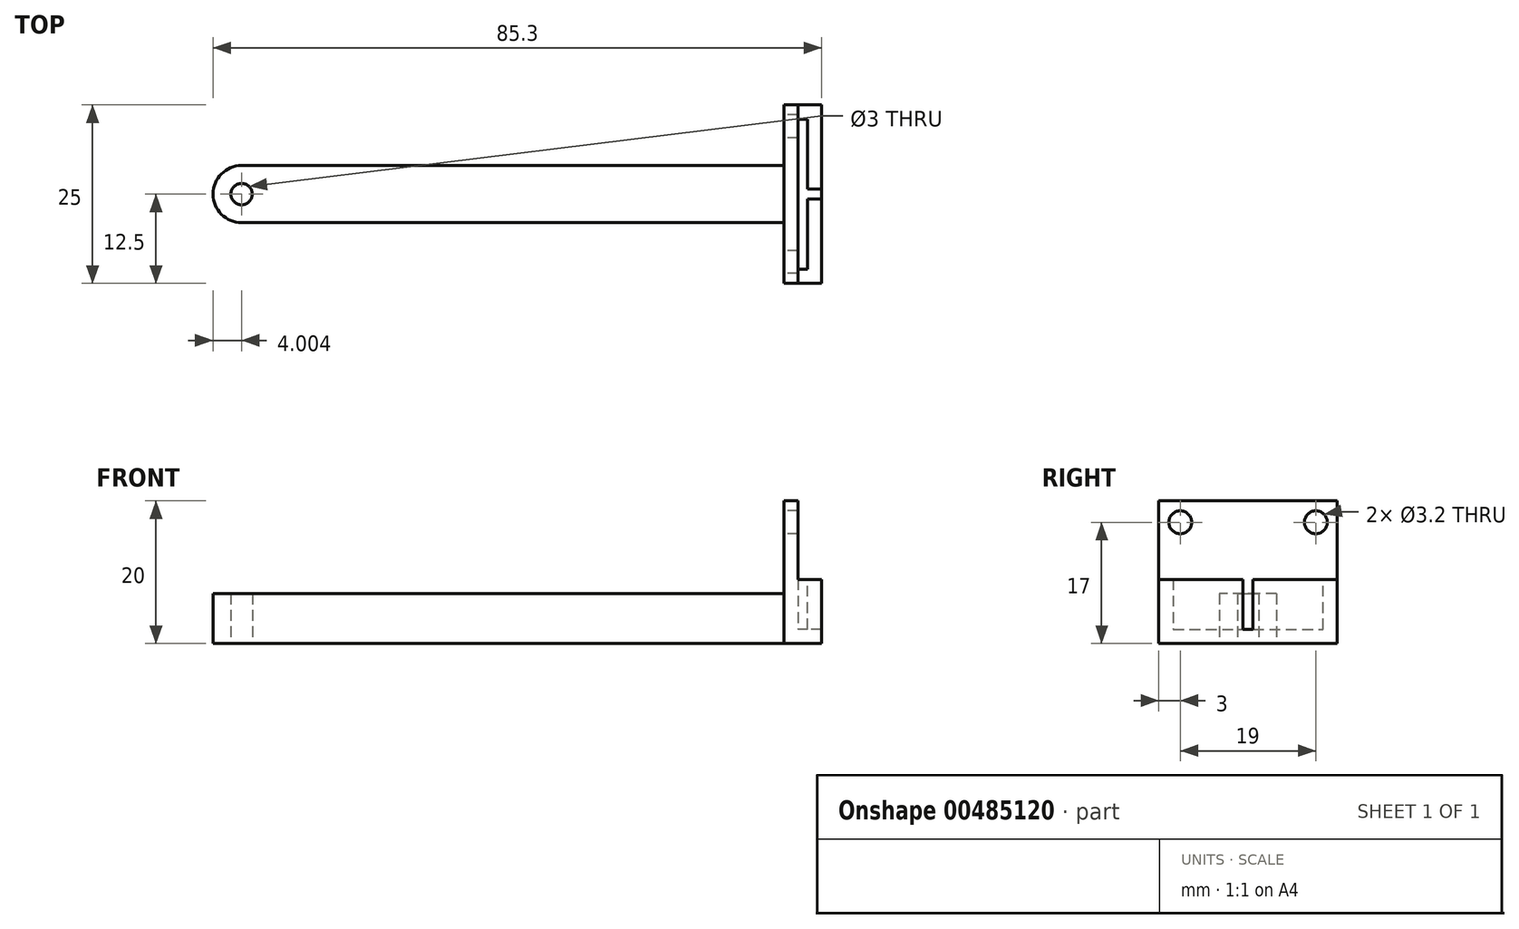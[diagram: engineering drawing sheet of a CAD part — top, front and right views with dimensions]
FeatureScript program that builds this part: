
annotation { "Feature Type Name" : "Feature", "Feature Type Description" : "" }
export const myFeature = defineFeature(function(context is Context, id is Id, definition is map)
    precondition{}
    {
        {
            var Q0;
            Q0=qCreatedBy(makeId("Top.planeOp"),FACE);
            var sketch = newSketch(context, id + "F0", { "sketchPlane" : qUnion([Q0])});
            skLineSegment(sketch, "E0.bottom", {"start": v(-63.58, 16) * mm, "end": v(16.42, 16) * mm});
            skLineSegment(sketch, "E0.top", {"start": v(-63.58, 8) * mm, "end": v(16.42, 8) * mm});
            skLineSegment(sketch, "E0.left", {"start": v(-63.58, 16) * mm, "end": v(-63.58, 8) * mm});
            skLineSegment(sketch, "E0.right", {"start": v(16.42, 16) * mm, "end": v(16.42, 8) * mm});
            skLineSegment(sketch, "E1", {"start": v(-55.58, 16) * mm, "end": v(-55.58, 8) * mm, "construction": true});
            skLineSegment(sketch, "E2", {"start": v(-63.58, 12) * mm, "end": v(-55.58, 12) * mm, "construction": true});
            skCircle(sketch, "E3", {"center": v(-59.58, 12) * mm, "radius": 1.5 * mm});
            skSolve(sketch);
        }
        {
            var Q0;
            Q0=makeQuery(id+"F0.imprint","IMPRINT",FACE,{"disambiguationData":[TD([[makeQuery(id+"F0.imprint","IMPRINT",EDGE,{"derivedFrom":sQuery(id+"F0.wireOp",EDGE,"E0.bottom")}),-1.0]])]});
            extrude(context, id + "F1", {"entities" : qUnion([Q0]), "depth" : 7 * mm, "offsetDistance" : 25 * mm});
        }
        {
            var Q0;
            Q0=makeQuery(id+"F1.opExtrude","SWEPT_EDGE",EDGE,{"disambiguationData":[OSD([sQuery(id+"F0.wireOp",EDGE,"E0.bottom"),sQuery(id+"F0.wireOp",EDGE,"E0.left")])]});
            var Q1;
            Q1=makeQuery(id+"F1.opExtrude","SWEPT_EDGE",EDGE,{"disambiguationData":[OSD([sQuery(id+"F0.wireOp",EDGE,"E0.top"),sQuery(id+"F0.wireOp",EDGE,"E0.left")])]});
            fillet(context, id + "F2", {"entities" : qUnion([Q0, Q1]), "radius" : 4 * mm, "tangentPropagation" : true, "allowEdgeOverflow" : false});
        }
        {
            var Q0;
            Q0=makeQuery(id+"F1.opExtrude","SWEPT_FACE",FACE,{"disambiguationData":[OSD([sQuery(id+"F0.wireOp",EDGE,"E0.right")])]});
            var sketch = newSketch(context, id + "F3", { "sketchPlane" : qUnion([Q0])});
            skLineSegment(sketch, "E4.bottom", {"start": v(24.5, 0) * mm, "end": v(-0.5, 0) * mm});
            skLineSegment(sketch, "E4.top", {"start": v(24.5, 20) * mm, "end": v(-0.5, 20) * mm});
            skLineSegment(sketch, "E4.left", {"start": v(24.5, 0) * mm, "end": v(24.5, 20) * mm});
            skLineSegment(sketch, "E4.right", {"start": v(-0.5, 0) * mm, "end": v(-0.5, 20) * mm});
            skLineSegment(sketch, "E5.bottom", {"start": v(8, 7) * mm, "end": v(16, 7) * mm, "construction": true});
            skLineSegment(sketch, "E5.top", {"start": v(8, 0) * mm, "end": v(16, 0) * mm, "construction": true});
            skLineSegment(sketch, "E5.left", {"start": v(8, 7) * mm, "end": v(8, 0) * mm, "construction": true});
            skLineSegment(sketch, "E5.right", {"start": v(16, 7) * mm, "end": v(16, 0) * mm, "construction": true});
            skLineSegment(sketch, "E6", {"start": v(-0.5, 17) * mm, "end": v(24.5, 17) * mm, "construction": true});
            skLineSegment(sketch, "E7", {"start": v(2.5, 20) * mm, "end": v(2.5, 0) * mm, "construction": true});
            skLineSegment(sketch, "E8", {"start": v(21.5, 20) * mm, "end": v(21.5, 0) * mm, "construction": true});
            skCircle(sketch, "E9", {"center": v(2.5, 17) * mm, "radius": 1 * mm, "construction": true});
            skCircle(sketch, "E10", {"center": v(21.5, 17) * mm, "radius": 1.35 * mm, "construction": true});
            skSolve(sketch);
        }
        {
            var Q0;
            Q0 = qSketchRegion(id + "F3", true);
            extrude(context, id + "F4", {"entities" : qUnion([Q0]), "operationType" : NewBodyOperationType.ADD, "depth" : 2 * mm, "offsetDistance" : 25 * mm});
        }
        {
            var Q0;
            Q0=makeQuery(id+"F4.opExtrude","CAP_FACE",FACE,{"disambiguationData":[OSD([sQuery(id+"F3.wireOp",EDGE,"E4.bottom"),sQuery(id+"F3.wireOp",EDGE,"E4.top"),sQuery(id+"F3.wireOp",EDGE,"E4.left"),sQuery(id+"F3.wireOp",EDGE,"E4.right")])],"isStart":false});
            var sketch = newSketch(context, id + "F5", { "sketchPlane" : qUnion([Q0])});
            skLineSegment(sketch, "E11.bottom", {"start": v(-0.5, 9) * mm, "end": v(24.5, 9) * mm, "construction": true});
            skLineSegment(sketch, "E11.top", {"start": v(-0.5, 0) * mm, "end": v(24.5, 0) * mm, "construction": true});
            skLineSegment(sketch, "E11.left", {"start": v(-0.5, 9) * mm, "end": v(-0.5, 0) * mm, "construction": true});
            skLineSegment(sketch, "E11.right", {"start": v(24.5, 9) * mm, "end": v(24.5, 0) * mm, "construction": true});
            skLineSegment(sketch, "E12", {"start": v(1.5, 9) * mm, "end": v(1.5, 0) * mm, "construction": true});
            skLineSegment(sketch, "E13", {"start": v(-0.5, 2) * mm, "end": v(24.5, 2) * mm, "construction": true});
            skLineSegment(sketch, "E14", {"start": v(22.5, 0) * mm, "end": v(22.5, 9) * mm, "construction": true});
            skLineSegment(sketch, "E15", {"start": v(-0.5, 9) * mm, "end": v(1.5, 9) * mm});
            skLineSegment(sketch, "E16", {"start": v(1.5, 9) * mm, "end": v(1.5, 2) * mm});
            skLineSegment(sketch, "E17", {"start": v(1.5, 2) * mm, "end": v(22.5, 2) * mm});
            skLineSegment(sketch, "E18", {"start": v(22.5, 2) * mm, "end": v(22.5, 9) * mm});
            skLineSegment(sketch, "E19", {"start": v(22.5, 9) * mm, "end": v(24.5, 9) * mm});
            skLineSegment(sketch, "E20", {"start": v(24.5, 9) * mm, "end": v(24.5, 0) * mm});
            skLineSegment(sketch, "E21", {"start": v(24.5, 0) * mm, "end": v(-0.5, 0) * mm});
            skLineSegment(sketch, "E22", {"start": v(-0.5, 0) * mm, "end": v(-0.5, 9) * mm});
            skSolve(sketch);
        }
        {
            var Q0;
            Q0=makeQuery(id+"F5.imprint","IMPRINT",FACE,{"disambiguationData":[TD([[makeQuery(id+"F5.imprint","IMPRINT",EDGE,{"derivedFrom":sQuery(id+"F5.wireOp",EDGE,"E15")}),-1.0]])]});
            extrude(context, id + "F6", {"entities" : qUnion([Q0]), "operationType" : NewBodyOperationType.ADD, "depth" : 1.3 * mm, "offsetDistance" : 25 * mm});
        }
        {
            var Q0;
            Q0=makeQuery(id+"F6.opExtrude","CAP_FACE",FACE,{"disambiguationData":[OSD([sQuery(id+"F5.wireOp",EDGE,"E15"),sQuery(id+"F5.wireOp",EDGE,"E16"),sQuery(id+"F5.wireOp",EDGE,"E17"),sQuery(id+"F5.wireOp",EDGE,"E18"),sQuery(id+"F5.wireOp",EDGE,"E19"),sQuery(id+"F5.wireOp",EDGE,"E20"),sQuery(id+"F5.wireOp",EDGE,"E21"),sQuery(id+"F5.wireOp",EDGE,"E22")])],"isStart":false});
            var sketch = newSketch(context, id + "F7", { "sketchPlane" : qUnion([Q0])});
            skLineSegment(sketch, "E23.bottom", {"start": v(-0.5, 9) * mm, "end": v(24.5, 9) * mm, "construction": true});
            skLineSegment(sketch, "E23.top", {"start": v(-0.5, 0) * mm, "end": v(24.5, 0) * mm, "construction": true});
            skLineSegment(sketch, "E23.left", {"start": v(-0.5, 9) * mm, "end": v(-0.5, 0) * mm, "construction": true});
            skLineSegment(sketch, "E23.right", {"start": v(24.5, 9) * mm, "end": v(24.5, 0) * mm, "construction": true});
            skLineSegment(sketch, "E24", {"start": v(11.3, 9) * mm, "end": v(11.3, 2) * mm, "construction": true});
            skLineSegment(sketch, "E25", {"start": v(11.3, 2) * mm, "end": v(12.7, 2) * mm, "construction": true});
            skLineSegment(sketch, "E26", {"start": v(12.7, 2) * mm, "end": v(12.7, 9) * mm, "construction": true});
            skLineSegment(sketch, "E27", {"start": v(-0.5, 9) * mm, "end": v(11.3, 9) * mm});
            skLineSegment(sketch, "E28", {"start": v(11.3, 2) * mm, "end": v(11.3, 9) * mm});
            skLineSegment(sketch, "E29", {"start": v(11.3, 2) * mm, "end": v(12.7, 2) * mm});
            skLineSegment(sketch, "E30", {"start": v(12.7, 2) * mm, "end": v(12.7, 9) * mm});
            skLineSegment(sketch, "E31", {"start": v(12.7, 9) * mm, "end": v(24.5, 9) * mm});
            skLineSegment(sketch, "E32", {"start": v(24.5, 9) * mm, "end": v(24.5, 0) * mm});
            skLineSegment(sketch, "E33", {"start": v(24.5, 0) * mm, "end": v(-0.5, 0) * mm});
            skLineSegment(sketch, "E34", {"start": v(-0.5, 0) * mm, "end": v(-0.5, 9) * mm});
            skSolve(sketch);
        }
        {
            var Q0;
            Q0 = qSketchRegion(id + "F7", true);
            extrude(context, id + "F8", {"entities" : qUnion([Q0]), "operationType" : NewBodyOperationType.ADD, "depth" : 2 * mm, "offsetDistance" : 25 * mm});
        }
        {
            var Q0;
            Q0=sQuery(id+"F3.wireOp",VERTEX,"E9.center");
            var Q1;
            Q1=sQuery(id+"F3.wireOp",VERTEX,"E10.center");
            var Q2;
            Q2=makeQuery(id+"F1.opExtrude","SWEPT_BODY",BODY,{"disambiguationData":[OSD([sQuery(id+"F0.wireOp",EDGE,"E0.bottom"),sQuery(id+"F0.wireOp",EDGE,"E0.top"),sQuery(id+"F0.wireOp",EDGE,"E0.left"),sQuery(id+"F0.wireOp",EDGE,"E0.right"),sQuery(id+"F0.wireOp",EDGE,"E3")])]});
            hole(context, id + "F9", {"style" : HoleStyle.SIMPLE, "endStyle" : HoleEndStyle.BLIND, "oppositeDirection" : true, "holeDiameter" : 3.2 * mm, "holeDepth" : 6 * mm, "isTappedThrough" : true, "tappedDepth" : 12 * mm, "tapClearance" : 3, "locations" : qUnion([Q0, Q1]), "scope" : qUnion([Q2])});
        }
    });
